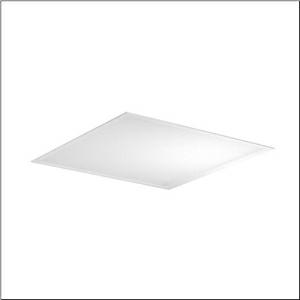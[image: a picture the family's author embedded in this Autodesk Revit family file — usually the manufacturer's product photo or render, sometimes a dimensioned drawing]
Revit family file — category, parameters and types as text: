
# Revit family: apollon_r__31_square_51mp12wd2m42_b676
name_source: partatom
category: Lighting Fixtures
units: mm (PartAtom-declared; Revit-internal decimal feet)

## family parameters
Cut with Voids When Loaded = No
Host = Face
Light Source = No
Part Type = Normal
Room Calculation Point = No
Round Connector Dimension = Use Diameter
Shared = No

## types (1)
- --- (1 x LED, 4000 lm, 27.5 W, 4000K)
    Apparent Load = 28 VA
    CIE Flux Codes = 62 87 97 100 100
    Color Rendering = 80
    Color Temperature = 4000K
    Default Elevation = 1800 mm
    Description = Apollon® 31 square, office luminaire, primary optical cover: micro prismatic cover, of PMMA, CAT 2 (L<= 3000cd/m²), light emission: direct distribution, primary light characteristic: symmetric, installation type: lay-in mounting, LED, rated luminous flux: 4.000lm, luminous efficacy: 142lm/W, light colour: 830/840, colour temperature: 3000/4000K, control gear: DALI 2, Multilumen, with terminal, 5-pole, mains connection: 220..240V, AC/DC, 0/50..60Hz, rated input power: 28W, housing, of aluminium, traffic white (RAL 9016), module: M600, length: 595mm, width: 595mm, height: 62mm, recess depth: 180mm, housing upper side, of sheet steel, coated, protection rating (complete): IP20, protection rating (on room side): IP40, insulation class (complete): insulation class II (safety insulation), certification: CE, ENEC, impact resistance: IK03, permissible operating ambient temperature: -20..+40°C, permissible storage temperature: -20..+60°C, standard: EN 60598-2-22, packaging unit: 1 piece
    Height = 0 mm  [stored 0 ft]
    Lamp = 1 x LED
    Lamp Light Flux = 4000 lm
    Lamp Power = 27.5 W
    Lamp count = 1
    Length = 595 mm
    Luminous efficacy = 145 lm/W
    Manufacturer = Siteco
    ModVariant = No
    Model = 51MP12WD2M42
    Mounting Place = Ceiling
    Mounting Type = Recessed
    Number of Poles = 1
    OnlyDefault = Yes
    Power Factor = 1
    Product Name = Apollon® 31 square
    Product group = office luminaire | ceiling recessed
    ProductGroupID = 401
    Protection Class = Protection class II
    Protection Degree = IP 20
    RLX_Detail_Level = 1
    RLX_Emergency_Light_Flux = 0 lm
    RLX_Emergency_Type = 0
    RLX_Emergency_Type_DB = No
    RlxData = <blob elided: 12817 chars, md5=6ca2d719>
    Socket = socket
    Standby Power = 0 W
    System Light Flux = 4000 lm
    System Power = 28 W
    Type Comments = factory setting: colour temperature 4000K
    Type Image = l_1291035.jpg
    URL = http://relux.com
    VarID = @adj_076624
    Voltage = 0 V
    Weight = 0.00 kg
    Width = 595 mm

note: [stored X ft] marks values corroborated as IEEE doubles in the binary element streams (Revit-internal decimal feet)

## geometry (parser evidence)
native form markers: Sweep x10
no freeform markers — native parametric forms only
